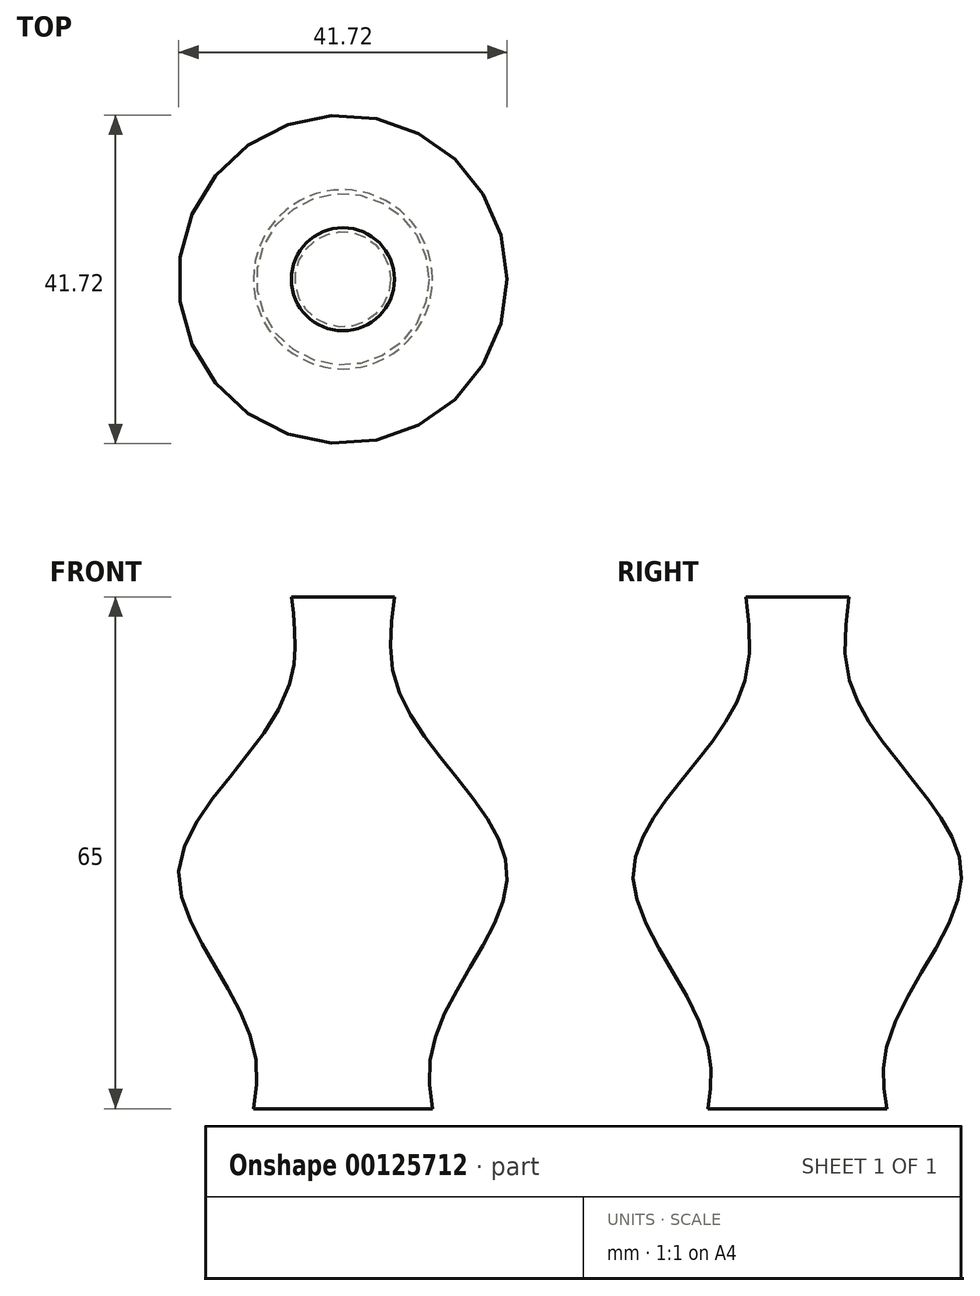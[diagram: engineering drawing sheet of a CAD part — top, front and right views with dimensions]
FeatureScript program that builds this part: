
annotation { "Feature Type Name" : "Feature", "Feature Type Description" : "" }
export const myFeature = defineFeature(function(context is Context, id is Id, definition is map)
    precondition{}
    {
        {
            var Q0;
            Q0=qCreatedBy(makeId("Top.planeOp"),FACE);
            cPlane(context, id + "F0", {"entities" : qUnion([Q0]), "cplaneType" : CPlaneType.OFFSET, "offset" : 5 * mm, "width" : 150 * mm, "height" : 150 * mm});
        }
        {
            var Q0;
            Q0=qCreatedBy(id+"F0.planeOp",FACE);
            cPlane(context, id + "F1", {"entities" : qUnion([Q0]), "cplaneType" : CPlaneType.OFFSET, "offset" : 25 * mm, "width" : 150 * mm, "height" : 150 * mm});
        }
        {
            var Q0;
            Q0=qCreatedBy(id+"F1.planeOp",FACE);
            cPlane(context, id + "F2", {"entities" : qUnion([Q0]), "cplaneType" : CPlaneType.OFFSET, "offset" : 25 * mm, "width" : 150 * mm, "height" : 150 * mm});
        }
        {
            var Q0;
            Q0=qCreatedBy(makeId("Top.planeOp"),FACE);
            var sketch = newSketch(context, id + "F3", { "sketchPlane" : qUnion([Q0])});
            skCircle(sketch, "E0", {"center": v(0, 0) * mm, "radius": 11.37 * mm});
            skSolve(sketch);
        }
        {
            var Q0;
            Q0=qCreatedBy(id+"F0.planeOp",FACE);
            var sketch = newSketch(context, id + "F4", { "sketchPlane" : qUnion([Q0])});
            skCircle(sketch, "E1", {"center": v(0, 0) * mm, "radius": 10.93 * mm});
            skSolve(sketch);
        }
        {
            var Q0;
            Q0=qCreatedBy(id+"F1.planeOp",FACE);
            var sketch = newSketch(context, id + "F5", { "sketchPlane" : qUnion([Q0])});
            skCircle(sketch, "E2", {"center": v(0, 0) * mm, "radius": 20.86 * mm});
            skSolve(sketch);
        }
        {
            var Q0;
            Q0=qCreatedBy(id+"F2.planeOp",FACE);
            var sketch = newSketch(context, id + "F6", { "sketchPlane" : qUnion([Q0])});
            skCircle(sketch, "E3", {"center": v(0, 0) * mm, "radius": 6.47 * mm});
            skSolve(sketch);
        }
        {
            var Q0;
            Q0=qCreatedBy(id+"F2.planeOp",FACE);
            cPlane(context, id + "F7", {"entities" : qUnion([Q0]), "cplaneType" : CPlaneType.OFFSET, "offset" : 10 * mm, "width" : 150 * mm, "height" : 150 * mm});
        }
        {
            var Q0;
            Q0=qCreatedBy(id+"F7.planeOp",FACE);
            var sketch = newSketch(context, id + "F8", { "sketchPlane" : qUnion([Q0])});
            skCircle(sketch, "E4", {"center": v(0, 0) * mm, "radius": 6.55 * mm});
            skSolve(sketch);
        }
        {
            var Q0;
            Q0 = qSketchRegion(id + "F3", true);
            var Q1;
            Q1 = qSketchRegion(id + "F4", true);
            var Q2;
            Q2 = qSketchRegion(id + "F5", true);
            var Q3;
            Q3 = qSketchRegion(id + "F6", true);
            var Q4;
            Q4 = qSketchRegion(id + "F8", true);
            loft(context, id + "F9", {"sheetProfilesArray" : [{ "sheetProfileEntities" : qUnion([Q0]) }, { "sheetProfileEntities" : qUnion([Q1]) }, { "sheetProfileEntities" : qUnion([Q2]) }, { "sheetProfileEntities" : qUnion([Q3]) }, { "sheetProfileEntities" : qUnion([Q4]) }]});
        }
    });
